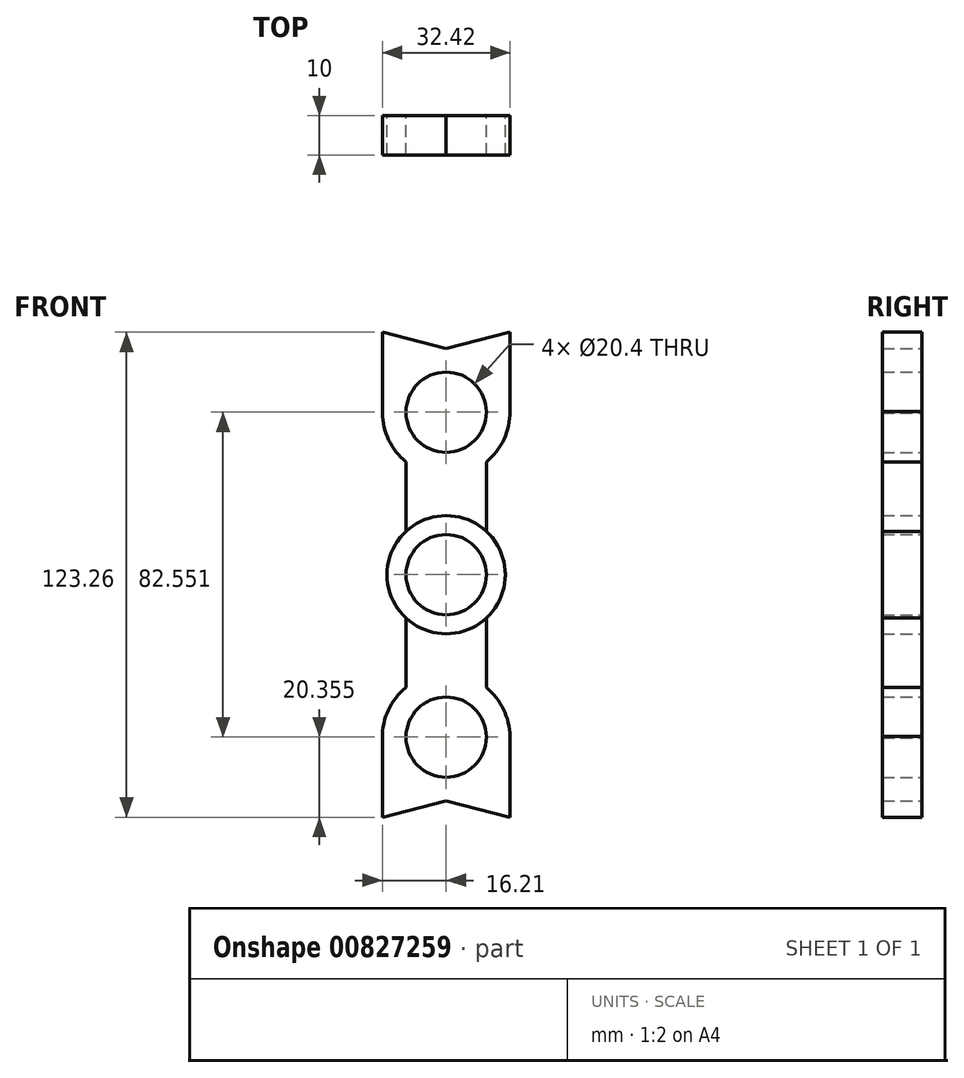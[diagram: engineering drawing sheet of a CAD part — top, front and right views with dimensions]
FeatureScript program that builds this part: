
annotation { "Feature Type Name" : "Feature", "Feature Type Description" : "" }
export const myFeature = defineFeature(function(context is Context, id is Id, definition is map)
    precondition{}
    {
        {
            var Q0;
            Q0=qCreatedBy(makeId("Front.planeOp"),FACE);
            var sketch = newSketch(context, id + "F0", { "sketchPlane" : qUnion([Q0])});
            skArc(sketch, "E0", {"start": v(10.2, 28.67) * mm, "mid": v(15.28, 46.69) * mm, "end": v(0, 57.49) * mm});
            skLineSegment(sketch, "E1.top", {"start": v(-10.2, 28.67) * mm, "end": v(-10.2, 28.67) * mm});
            skLineSegment(sketch, "E1.left", {"start": v(-10.2, 11.02) * mm, "end": v(-10.2, 28.67) * mm});
            skLineSegment(sketch, "E1.right", {"start": v(10.2, 11.02) * mm, "end": v(10.2, 28.67) * mm});
            skCircle(sketch, "E2", {"center": v(0, 41.28) * mm, "radius": 10.2 * mm});
            skLineSegment(sketch, "E3", {"start": v(-16.21, 41.06) * mm, "end": v(-16.21, 61.63) * mm});
            skLineSegment(sketch, "E4", {"start": v(-16.21, 61.63) * mm, "end": v(0, 57.49) * mm});
            skArc(sketch, "E5.trimOffspring", {"start": v(-16.21, 41.06) * mm, "mid": v(-14.59, 34.2) * mm, "end": v(-10.2, 28.67) * mm});
            skLineSegment(sketch, "E6.MirrorCS", {"start": v(16.21, 41.06) * mm, "end": v(16.21, 61.63) * mm});
            skLineSegment(sketch, "E7.MirrorCS", {"start": v(16.21, 61.63) * mm, "end": v(0, 57.49) * mm});
            skArc(sketch, "E8", {"start": v(-10.2, 11.02) * mm, "mid": v(0, -15.02) * mm, "end": v(10.2, 11.02) * mm});
            skPoint(sketch, "E1.bottom.start.orphan", {"position": v(-10.2, 0) * mm});
            skCircle(sketch, "E9", {"center": v(0, 0) * mm, "radius": 10.2 * mm});
            skSolve(sketch);
        }
        {
            var Q0;
            Q0=qSketchRegion(id+"F0",true);
            extrude(context, id + "F1", {"entities" : qUnion([Q0]), "depth" : 10 * mm, "offsetDistance" : 25.4 * mm});
        }
        {
            var Q0;
            Q0=qCreatedBy(makeId("Top.planeOp"),FACE);
            var sketch = newSketch(context, id + "F2", { "sketchPlane" : qUnion([Q0])});
            skLineSegment(sketch, "E10", {"start": v(0, 0) * mm, "end": v(0, -64.36) * mm, "construction": true});
            skSolve(sketch);
        }
        {
            var Q0;
            Q0=makeQuery(id+"F1.opExtrude","SWEPT_BODY",BODY,{"disambiguationData":[OSD([sQuery(id+"F0.wireOp",EDGE,"E0"),sQuery(id+"F0.wireOp",EDGE,"E1.left"),sQuery(id+"F0.wireOp",EDGE,"E1.right"),sQuery(id+"F0.wireOp",EDGE,"E2"),sQuery(id+"F0.wireOp",EDGE,"E3"),sQuery(id+"F0.wireOp",EDGE,"E4"),sQuery(id+"F0.wireOp",EDGE,"E5.trimOffspring"),sQuery(id+"F0.wireOp",EDGE,"E6.MirrorCS"),sQuery(id+"F0.wireOp",EDGE,"E7.MirrorCS"),sQuery(id+"F0.wireOp",EDGE,"E8"),sQuery(id+"F0.wireOp",EDGE,"E9")])]});
            var Q1;
            Q1=sQuery(id+"F2.wireOp",EDGE,"E10");
            circularPattern(context, id + "F3", {"entities" : qUnion([Q0]), "axis" : qUnion([Q1]), "angle" : 180 * degree, "instanceCount" : 2, "equalSpace" : true});
        }
    });
